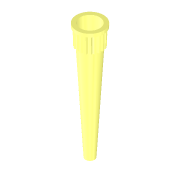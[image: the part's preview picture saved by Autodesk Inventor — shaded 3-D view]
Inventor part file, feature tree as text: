
AUTODESK INVENTOR PART (.ipt)
format: ipt  version: 2022 (Build 260153000, 153)  size: 240,128 bytes
history: native  units: mm
features: extrude x1, sketch x1
ambient origin geometry x8: Origin, YZ Plane, XZ Plane, XY Plane, X Axis, Y Axis, Z Axis, Center Point
bodies: Solid2 (feature_tree), Solid1 (feature_tree)
feature tree (2):
  extrude  "Extrusion1"  [1 undecoded]
  sketch  "Sketch1"  dims[d0=13.0mm d1=0.0mm]
note: 1 required parameter value undecoded (feature->parameter linkage not recoverable at this tier; creation-order binding heuristic only, values carry confidence <= 0.55)
